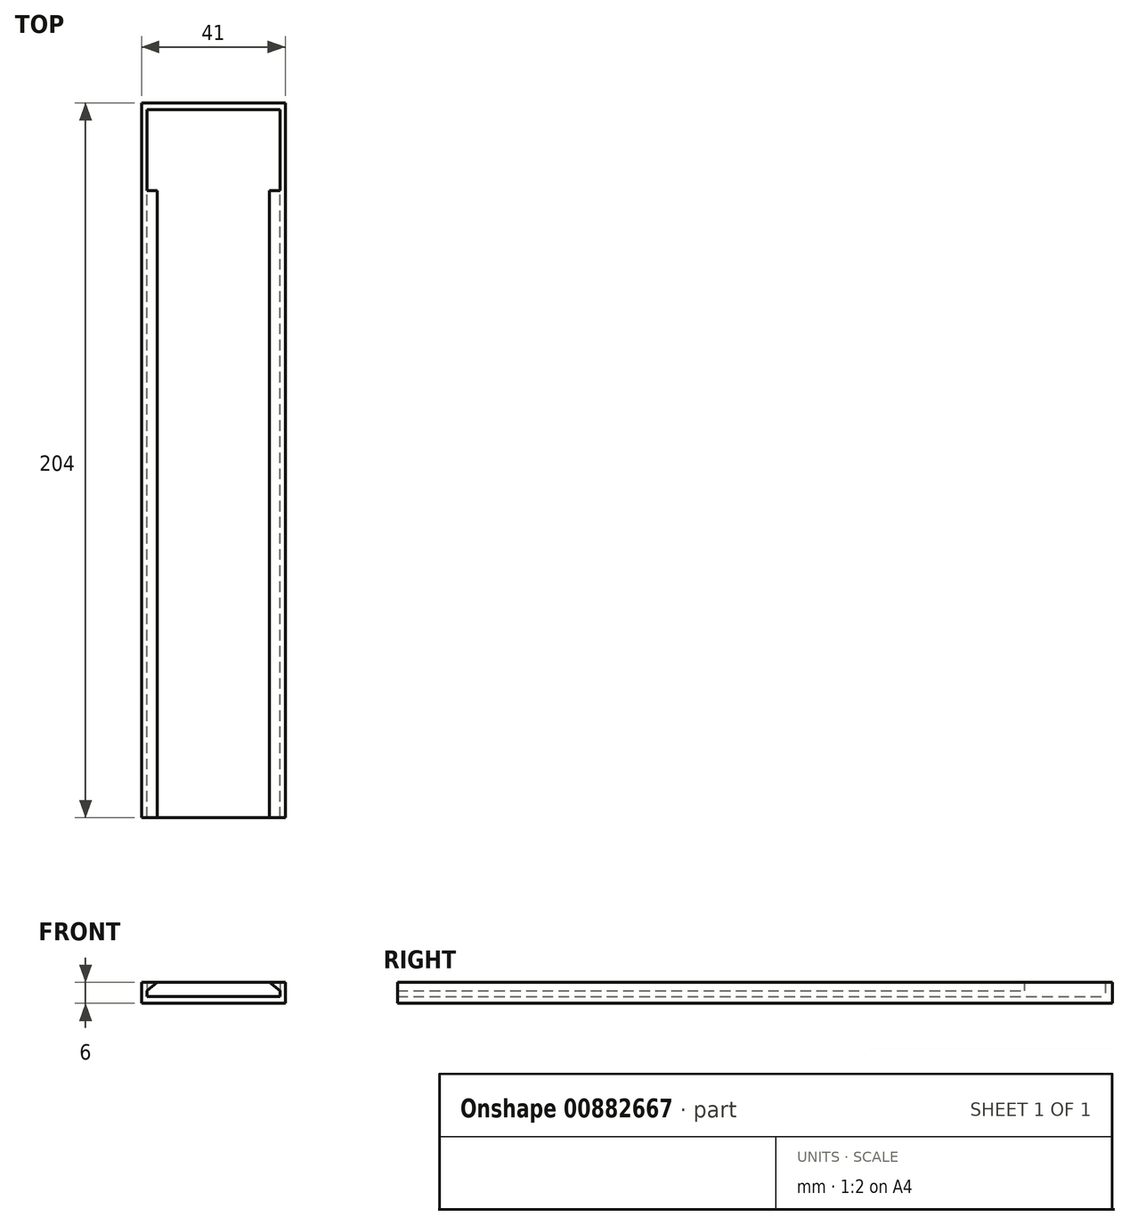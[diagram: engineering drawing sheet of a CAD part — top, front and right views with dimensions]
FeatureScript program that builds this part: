
annotation { "Feature Type Name" : "Feature", "Feature Type Description" : "" }
export const myFeature = defineFeature(function(context is Context, id is Id, definition is map)
    precondition{}
    {
        {
            var Q0;
            Q0=qCreatedBy(makeId("Front.planeOp"),FACE);
            var sketch = newSketch(context, id + "F0", { "sketchPlane" : qUnion([Q0])});
            skLineSegment(sketch, "E0", {"start": v(-20.5, 0) * mm, "end": v(20.5, 0) * mm});
            skLineSegment(sketch, "E1", {"start": v(20.5, 0) * mm, "end": v(20.5, 6) * mm});
            skLineSegment(sketch, "E2", {"start": v(20.5, 6) * mm, "end": v(16, 6) * mm});
            skLineSegment(sketch, "E3", {"start": v(19, 2) * mm, "end": v(-19, 2) * mm});
            skLineSegment(sketch, "E4", {"start": v(-16, 6) * mm, "end": v(-20.5, 6) * mm});
            skLineSegment(sketch, "E5", {"start": v(-20.5, 6) * mm, "end": v(-20.5, 0) * mm});
            skLineSegment(sketch, "E6", {"start": v(-16, 6) * mm, "end": v(16, 6) * mm});
            skLineSegment(sketch, "E7", {"start": v(16, 6) * mm, "end": v(19, 3.6) * mm});
            skLineSegment(sketch, "E8", {"start": v(19, 3.6) * mm, "end": v(19, 2) * mm});
            skLineSegment(sketch, "E9", {"start": v(-16, 6) * mm, "end": v(-19, 3.6) * mm});
            skLineSegment(sketch, "E10", {"start": v(-19, 3.6) * mm, "end": v(-19, 2) * mm});
            skSolve(sketch);
        }
        {
            var Q0;
            Q0=makeQuery(id+"F0.imprint","IMPRINT",FACE,{"disambiguationData":[TD([[makeQuery(id+"F0.imprint","IMPRINT",EDGE,{"derivedFrom":sQuery(id+"F0.wireOp",EDGE,"E0")}),1.0]])]});
            extrude(context, id + "F1", {"entities" : qUnion([Q0]), "depth" : 202 * mm, "offsetDistance" : 25 * mm});
        }
        {
            var Q0;
            Q0=qCreatedBy(makeId("Front.planeOp"),FACE);
            var sketch = newSketch(context, id + "F2", { "sketchPlane" : qUnion([Q0])});
            skLineSegment(sketch, "E11.bottom", {"start": v(20.5, 6) * mm, "end": v(-20.5, 6) * mm});
            skLineSegment(sketch, "E11.top", {"start": v(20.5, 0) * mm, "end": v(-20.5, 0) * mm});
            skLineSegment(sketch, "E11.left", {"start": v(20.5, 6) * mm, "end": v(20.5, 0) * mm});
            skLineSegment(sketch, "E11.right", {"start": v(-20.5, 6) * mm, "end": v(-20.5, 0) * mm});
            skSolve(sketch);
        }
        {
            var Q0;
            Q0=makeQuery(id+"F2.imprint","IMPRINT",FACE,{"disambiguationData":[TD([[makeQuery(id+"F2.imprint","IMPRINT",EDGE,{"derivedFrom":sQuery(id+"F2.wireOp",EDGE,"E11.bottom")}),1.0]])]});
            extrude(context, id + "F3", {"entities" : qUnion([Q0]), "operationType" : NewBodyOperationType.ADD, "oppositeDirection" : true, "depth" : 2 * mm, "offsetDistance" : 25 * mm});
        }
        {
            var Q0;
            Q0=makeQuery(id+"F3.boolean.opBoolean","MERGE",FACE,{"derivedFrom":[makeQuery(id+"F1.opExtrude","SWEPT_FACE",FACE,{"disambiguationData":[OSD([sQuery(id+"F0.wireOp",EDGE,"E2")])]}),makeQuery(id+"F1.opExtrude","SWEPT_FACE",FACE,{"disambiguationData":[OSD([sQuery(id+"F0.wireOp",EDGE,"E4")])]}),makeQuery(id+"F3.opExtrude","SWEPT_FACE",FACE,{"disambiguationData":[OSD([sQuery(id+"F2.wireOp",EDGE,"E11.bottom")])]})]});
            cPlane(context, id + "F4", {"entities" : qUnion([Q0]), "cplaneType" : CPlaneType.OFFSET, "offset" : 0 * mm, "width" : 150 * mm, "height" : 150 * mm});
        }
        {
            var Q0;
            Q0=qCreatedBy(id+"F4.planeOp",FACE);
            var sketch = newSketch(context, id + "F5", { "sketchPlane" : qUnion([Q0])});
            skLineSegment(sketch, "E12.bottom", {"start": v(19, 0) * mm, "end": v(-19, 0) * mm});
            skLineSegment(sketch, "E12.top", {"start": v(19, -23) * mm, "end": v(-19, -23) * mm});
            skLineSegment(sketch, "E12.left", {"start": v(19, 0) * mm, "end": v(19, -23) * mm});
            skLineSegment(sketch, "E12.right", {"start": v(-19, 0) * mm, "end": v(-19, -23) * mm});
            skSolve(sketch);
        }
        {
            var Q0;
            Q0=makeQuery(id+"F5.imprint","IMPRINT",FACE,{"disambiguationData":[TD([[makeQuery(id+"F5.imprint","IMPRINT",EDGE,{"derivedFrom":sQuery(id+"F5.wireOp",EDGE,"E12.bottom")}),1.0]])]});
            extrude(context, id + "F6", {"entities" : qUnion([Q0]), "operationType" : NewBodyOperationType.REMOVE, "oppositeDirection" : true, "depth" : 4 * mm, "offsetDistance" : 25 * mm});
        }
    });
